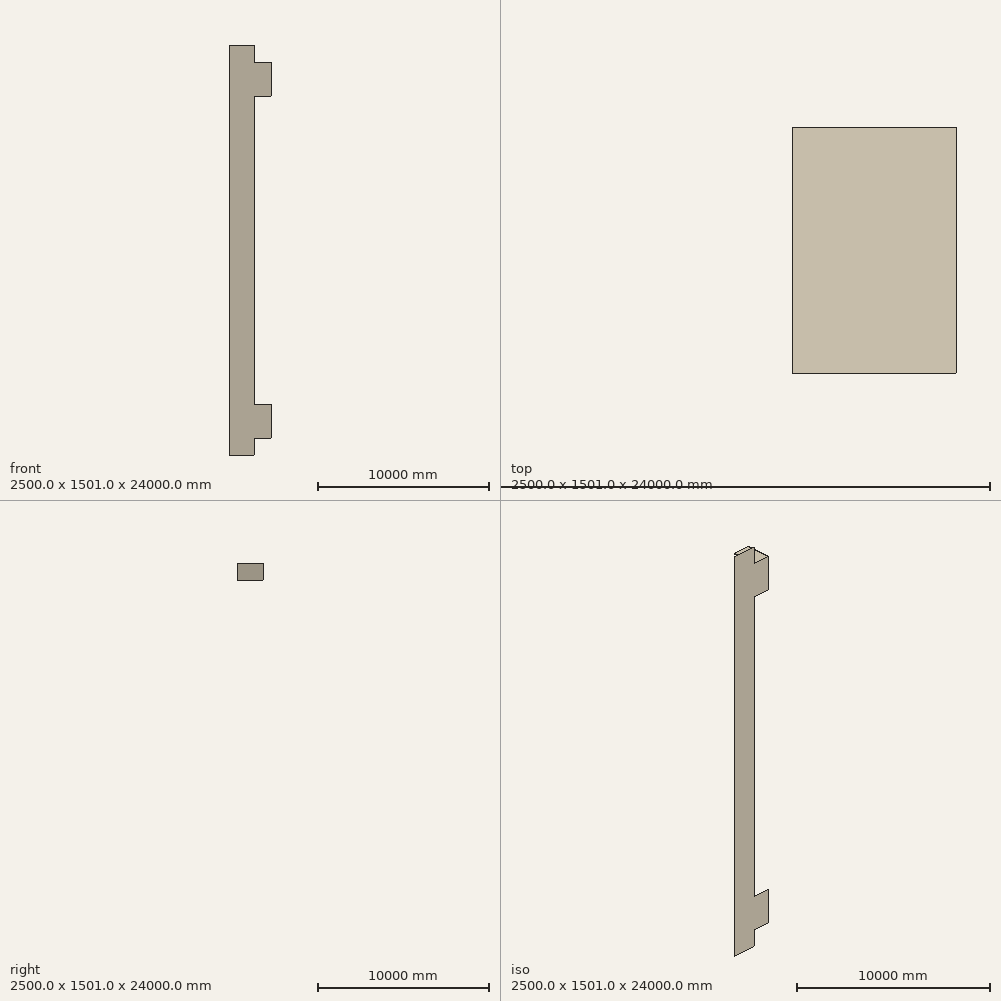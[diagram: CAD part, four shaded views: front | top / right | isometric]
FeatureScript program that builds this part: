
annotation { "Feature Type Name" : "Feature", "Feature Type Description" : "" }
export const myFeature = defineFeature(function(context is Context, id is Id, definition is map)
    precondition{}
    {
        {
            var Q0;
            Q0=qCreatedBy(makeId("Front.planeOp"),FACE);
            var sketch = newSketch(context, id + "F0", { "sketchPlane" : qUnion([Q0])});
            skLineSegment(sketch, "E0", {"start": v(-2366.53, 11814.38) * mm, "end": v(-2366.53, -12185.62) * mm});
            skLineSegment(sketch, "E1", {"start": v(-2366.53, -12185.62) * mm, "end": v(-866.53, -12185.62) * mm});
            skLineSegment(sketch, "E2", {"start": v(-866.53, -12185.62) * mm, "end": v(-866.53, -11185.62) * mm});
            skLineSegment(sketch, "E3", {"start": v(-866.53, -11185.62) * mm, "end": v(133.47, -11185.62) * mm});
            skLineSegment(sketch, "E4", {"start": v(133.47, -11185.62) * mm, "end": v(133.47, -9185.62) * mm});
            skLineSegment(sketch, "E5", {"start": v(133.47, -9185.62) * mm, "end": v(-866.53, -9185.62) * mm});
            skLineSegment(sketch, "E6", {"start": v(-866.53, -9185.62) * mm, "end": v(-866.53, 8814.38) * mm});
            skLineSegment(sketch, "E7", {"start": v(-866.53, 8814.38) * mm, "end": v(133.47, 8814.38) * mm});
            skLineSegment(sketch, "E8", {"start": v(133.47, 8814.38) * mm, "end": v(133.47, 10814.38) * mm});
            skLineSegment(sketch, "E9", {"start": v(133.47, 10814.38) * mm, "end": v(-866.53, 10814.38) * mm});
            skLineSegment(sketch, "E10", {"start": v(-866.53, 10814.38) * mm, "end": v(-866.53, 11814.38) * mm});
            skLineSegment(sketch, "E11", {"start": v(-866.53, 11814.38) * mm, "end": v(-2366.53, 11814.38) * mm});
            skSolve(sketch);
        }
        {
            var Q0;
            Q0 = qSketchRegion(id + "F0", true);
            extrude(context, id + "F1", {"entities" : qUnion([Q0]), "depth" : 1 * mm, "offsetDistance" : 25 * mm});
        }
        {
            var Q0;
            Q0=makeQuery(id+"F1.opExtrude","CAP_FACE",FACE,{"disambiguationData":[OSD([sQuery(id+"F0.wireOp",EDGE,"E0"),sQuery(id+"F0.wireOp",EDGE,"E1"),sQuery(id+"F0.wireOp",EDGE,"E2"),sQuery(id+"F0.wireOp",EDGE,"E3"),sQuery(id+"F0.wireOp",EDGE,"E4"),sQuery(id+"F0.wireOp",EDGE,"E5"),sQuery(id+"F0.wireOp",EDGE,"E6"),sQuery(id+"F0.wireOp",EDGE,"E7"),sQuery(id+"F0.wireOp",EDGE,"E8"),sQuery(id+"F0.wireOp",EDGE,"E9"),sQuery(id+"F0.wireOp",EDGE,"E10"),sQuery(id+"F0.wireOp",EDGE,"E11")])],"isStart":true});
            var sketch = newSketch(context, id + "F2", { "sketchPlane" : qUnion([Q0])});
            skLineSegment(sketch, "E12.bottom", {"start": v(866.53, 10814.38) * mm, "end": v(-133.47, 10814.38) * mm});
            skLineSegment(sketch, "E12.top", {"start": v(866.53, 10764.38) * mm, "end": v(-133.47, 10764.38) * mm});
            skLineSegment(sketch, "E12.left", {"start": v(866.53, 10814.38) * mm, "end": v(866.53, 10764.38) * mm});
            skLineSegment(sketch, "E12.right", {"start": v(-133.47, 10814.38) * mm, "end": v(-133.47, 10764.38) * mm});
            skPoint(sketch, "E13.oppositeSnap0", {"position": v(-133.47, 9814.38) * mm});
            skLineSegment(sketch, "E13.bottom", {"start": v(-133.47, 10764.38) * mm, "end": v(-83.47, 10764.38) * mm});
            skLineSegment(sketch, "E13.top", {"start": v(-133.47, 9814.38) * mm, "end": v(-83.47, 9814.38) * mm});
            skLineSegment(sketch, "E13.left", {"start": v(-133.47, 10764.38) * mm, "end": v(-133.47, 9814.38) * mm});
            skLineSegment(sketch, "E13.right", {"start": v(-83.47, 10764.38) * mm, "end": v(-83.47, 9814.38) * mm});
            skSolve(sketch);
        }
        {
            var Q0;
            Q0 = qSketchRegion(id + "F2", true);
            extrude(context, id + "F3", {"entities" : qUnion([Q0]), "depth" : 1500 * mm, "offsetDistance" : 25 * mm});
        }
    });
